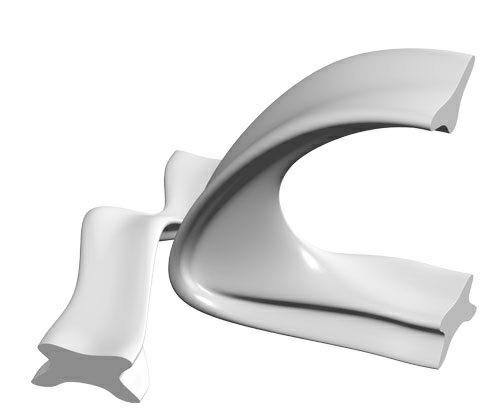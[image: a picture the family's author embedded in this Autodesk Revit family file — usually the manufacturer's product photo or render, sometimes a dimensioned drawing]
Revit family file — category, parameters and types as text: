
# Revit family: CITY ALPHABET litera „K”
name_source: partatom
category: Meble
revit_build: Autodesk Revit 2018 (Build: 20190510_1515(x64)
units: mm (PartAtom-declared; Revit-internal decimal feet)

## family parameters
Numer OmniClass = 23.40.10.11.14
Obiekt nadrzędny = Powierzchnia
Punkt obliczania pomieszczeń = Nie
Tnij formami wycięć po wczytaniu = Nie
Tytuł OmniClass = Exterior Seating
Współdzielony = Nie

## types (1)
- CITY ALPHABET litera „K”
    Domyślna rzędna = 1219 mm
    Długość = 2400 mm
    IfcExportAs = IfcFurnishingElement
    Komentarze do typu = Ławka
    Materiał - informacja = Szeroki wybór kolorów wg palety RAL. Istnieje również możliwość specjalnego wykonania
kolorystycznego na indywidualne zapytanie klienta.
    Model = CITY ALPHABET litera „K”
    Obraz typu = K.jpg
    Producent = Astrini Design
    Szerokość = 2400 mm
    Temepratura użytkowania = -40°C do 80°C, ( -40°F do 176°F )
    URL = http://astrini-design.pl
    Waga (szacunkowo) = 115.00 kg
    Waga po wypełnieniu (szacunkowo) = 215.00 kg
    Wysokość = 1900 mm  [stored 6.2336 ft]

note: [stored X ft] marks values corroborated as IEEE doubles in the binary element streams (Revit-internal decimal feet)
